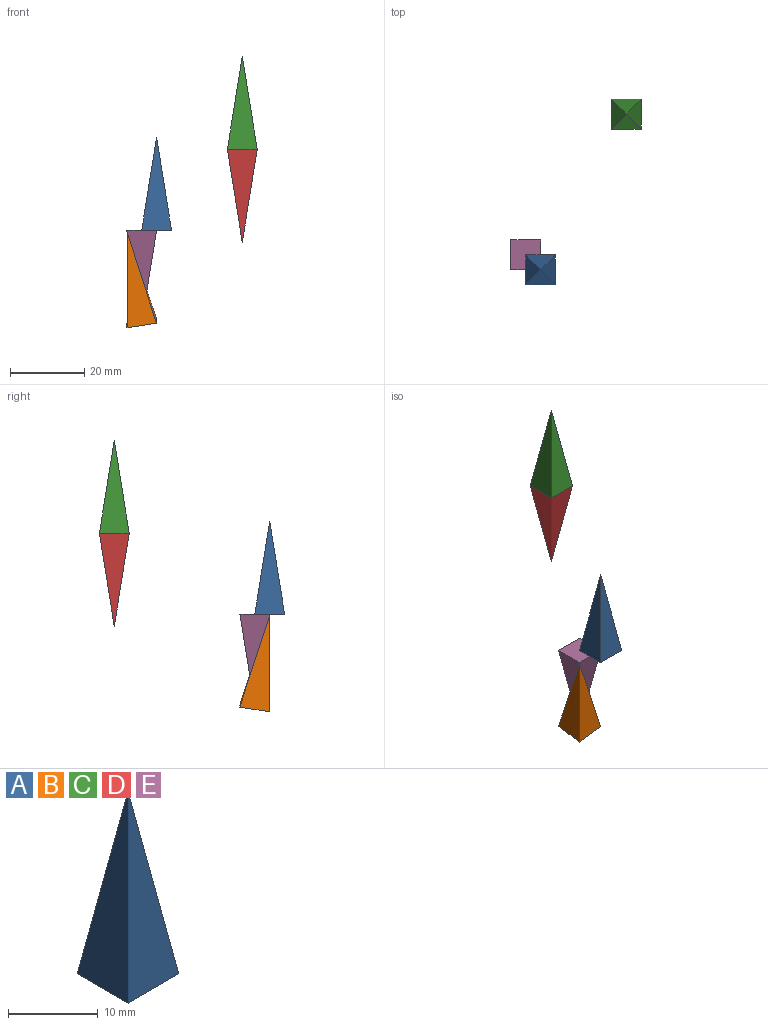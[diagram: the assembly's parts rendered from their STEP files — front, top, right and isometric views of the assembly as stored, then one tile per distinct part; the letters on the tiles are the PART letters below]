
ASSEMBLY  parts=5 mates=2
PART A: 5 faces, bbox 8x8x25 mm
  f0: plane 24.97x8mm, normal (-0.99,0,0.16), area 101.2mm2, adj f1,f3,f4
  f1: plane 24.97x8mm, normal (0,-0.99,0.16), area 101.2mm2, adj f0,f2,f4
  f2: plane 24.97x8mm, normal (0.99,0,0.16), area 101.2mm2, adj f1,f3,f4
  f3: plane 24.97x8mm, normal (0,0.99,0.16), area 101.2mm2, adj f0,f2,f4
  f4: plane 8x8mm, normal (0,0,-1), area 64mm2, adj f0,f1,f2,f3
PART B: same geometry as A
PART C: same geometry as A
PART D: same geometry as A
PART E: same geometry as A
PLACE A t=(-5.9,-32.18,-30.26)mm
PLACE B rot(axis=(0.71,-0.7,-0.06),12.8deg) t=(-9.9,-28.18,-55.24)mm
PLACE C t=(17.11,9.57,-8.53)mm
PLACE D rot(axis=(0.71,-0.71,0),180deg) t=(17.11,9.57,-8.53)mm
PLACE E rot(axis=(1,0,0),180deg) t=(-9.9,-28.18,-30.26)mm
MATE fastened D.f4 <-> C.f4  axis (0,0,-1) through (17.11,9.57,-8.53)mm
MATE fastened E.f4 <-> A.f4  axis (0,0,1) through (-5.9,-32.18,-30.26)mm
